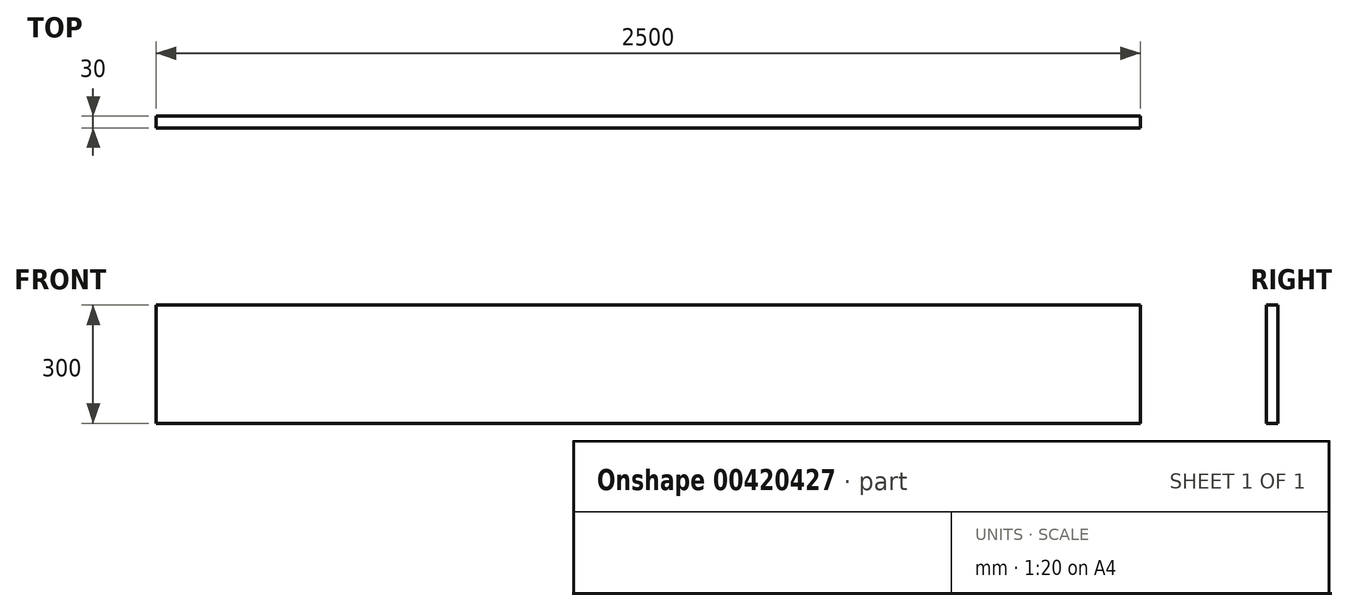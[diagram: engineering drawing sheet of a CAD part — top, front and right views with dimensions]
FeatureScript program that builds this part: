
annotation { "Feature Type Name" : "Feature", "Feature Type Description" : "" }
export const myFeature = defineFeature(function(context is Context, id is Id, definition is map)
    precondition{}
    {
        {
            var Q0;
            Q0=qCreatedBy(makeId("Front.planeOp"),FACE);
            var sketch = newSketch(context, id + "F0", { "sketchPlane" : qUnion([Q0])});
            skLineSegment(sketch, "E0.bottom", {"start": v(1250, -150) * mm, "end": v(-1250, -150) * mm});
            skLineSegment(sketch, "E0.top", {"start": v(1250, 150) * mm, "end": v(-1250, 150) * mm});
            skLineSegment(sketch, "E0.left", {"start": v(1250, -150) * mm, "end": v(1250, 150) * mm});
            skLineSegment(sketch, "E0.right", {"start": v(-1250, -150) * mm, "end": v(-1250, 150) * mm});
            skPoint(sketch, "E0.middle", {"position": v(0, 0) * mm});
            skSolve(sketch);
        }
        {
            var Q0;
            Q0=makeQuery(id+"F0.imprint","IMPRINT",FACE,{"disambiguationData":[TD([[makeQuery(id+"F0.imprint","IMPRINT",EDGE,{"derivedFrom":sQuery(id+"F0.wireOp",EDGE,"E0.bottom")}),-1.0]])]});
            extrude(context, id + "F1", {"entities" : qUnion([Q0]), "depth" : 30 * mm});
        }
    });
